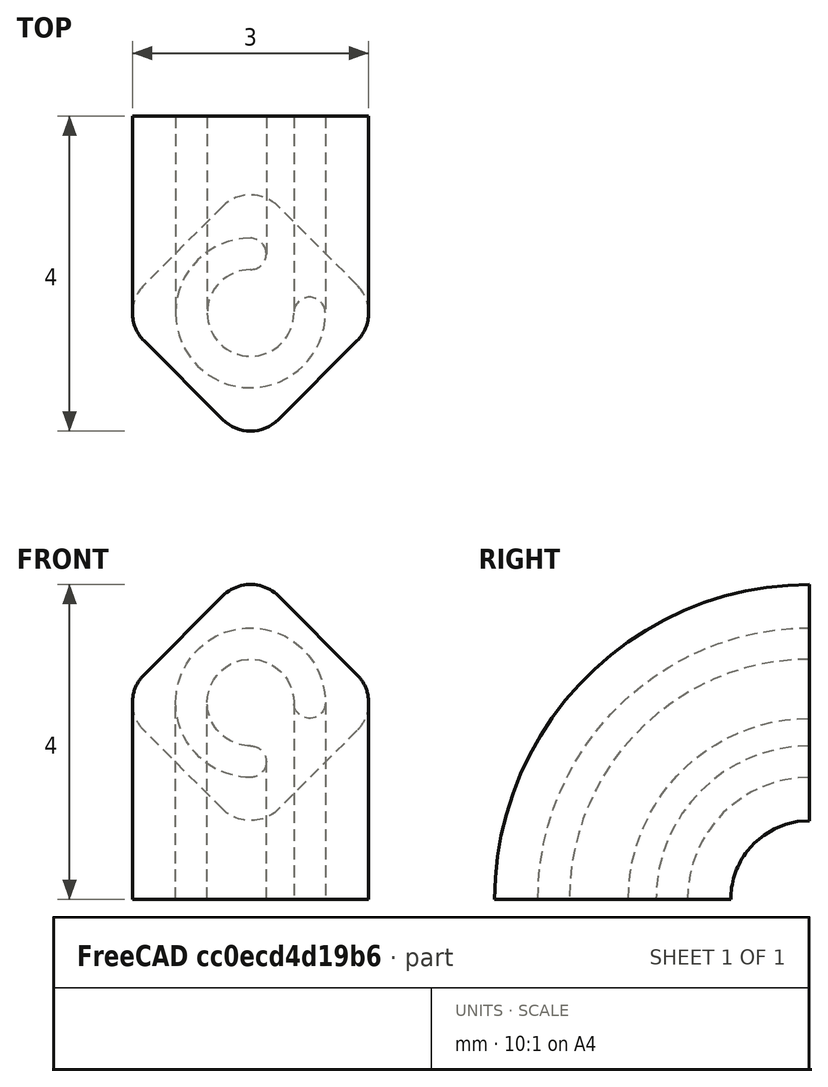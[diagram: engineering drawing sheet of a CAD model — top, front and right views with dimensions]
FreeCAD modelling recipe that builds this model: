
FCSTD DOCUMENT  (FreeCAD 1.0R39109 (Git))
Label: diffusor
License: All rights reserved
LicenseURL: https://en.wikipedia.org/wiki/All_rights_reserved
objects: Sketcher::SketchObject×2, App::VarSet×1, PartDesign::AdditivePipe×1, PartDesign::Body×1
note: 8 computed .brp shape members not serialized (recipe doc carries the construction recipe); baked Part::Feature solids carry a one-line shape summary decoded from their .brp

FEATURE [Sketcher::SketchObject] Sketch  label="diffusor section"
  ArcFitTolerance = 1e-06
  AttachmentSupport = -> [XY_Plane]
  FullyConstrained = true
  MakeInternals = false
  MapMode = 5
  expr: Constraints[11] = VarSet.extension * 0.5
  expr: Constraints[16] = VarSet.extension
  expr: Constraints[17] = VarSet.extension
  expr: Constraints[23] = VarSet.extension * 0.75
  expr: Constraints[24] = VarSet.extension * 0.2
  sketch-geometry (12):
    g0: LineSegment StartX=1.35355 StartY=0.353553 StartZ=0 EndX=0.353553 EndY=1.35355 EndZ=0
    g1: LineSegment StartX=-0.353553 StartY=1.35355 StartZ=0 EndX=-1.35355 EndY=0.353553 EndZ=0
    g2: LineSegment StartX=-1.35355 StartY=-0.353553 StartZ=0 EndX=-0.353553 EndY=-1.35355 EndZ=0
    g3: LineSegment StartX=0.353553 StartY=-1.35355 StartZ=0 EndX=1.35355 EndY=-0.353553 EndZ=0
    g4: ArcOfCircle CenterX=1 CenterY=0 CenterZ=0 NormalX=0 NormalY=0 NormalZ=1 AngleXU=0 Radius=0.5 StartAngle=5.49779 EndAngle=7.06858
    g5: ArcOfCircle CenterX=0 CenterY=1 CenterZ=0 NormalX=0 NormalY=0 NormalZ=1 AngleXU=0 Radius=0.5 StartAngle=0.785398 EndAngle=2.35619
    g6: ArcOfCircle CenterX=-1 CenterY=0 CenterZ=0 NormalX=0 NormalY=0 NormalZ=1 AngleXU=0 Radius=0.5 StartAngle=2.35619 EndAngle=3.92699
    g7: ArcOfCircle CenterX=0 CenterY=-1 CenterZ=0 NormalX=0 NormalY=0 NormalZ=1 AngleXU=0 Radius=0.5 StartAngle=3.92699 EndAngle=5.49779
    g8: ArcOfCircle CenterX=0 CenterY=0 CenterZ=0 NormalX=0 NormalY=0 NormalZ=1 AngleXU=0 Radius=0.95 StartAngle=1.5708 EndAngle=6.28319
    g9: ArcOfCircle CenterX=0.75 CenterY=0 CenterZ=0 NormalX=0 NormalY=0 NormalZ=1 AngleXU=0 Radius=0.2 StartAngle=-4.237e-13 EndAngle=3.14159
    g10: ArcOfCircle CenterX=0 CenterY=0.75 CenterZ=0 NormalX=0 NormalY=0 NormalZ=1 AngleXU=0 Radius=0.2 StartAngle=4.71239 EndAngle=7.85398
    g11: ArcOfCircle CenterX=0 CenterY=0 CenterZ=0 NormalX=0 NormalY=0 NormalZ=1 AngleXU=0 Radius=0.55 StartAngle=1.5708 EndAngle=6.28319
  constraints (28):
    c: Tangent(g0,g4) = -1.5708
    c: Tangent(g0,g5) = -1.5708
    c: Tangent(g1,g5) = -1.5708
    c: Tangent(g1,g6) = -1.5708
    c: Tangent(g2,g6) = -1.5708
    c: Tangent(g2,g7) = -1.5708
    c: Tangent(g3,g7) = -1.5708
    c: Tangent(g3,g4) = -1.5708
    c: Parallel(g0,g2)
    c: Parallel(g1,g3)
    c: Equal(g4,g5)
    c: Radius(g5) = 0.5
    c: Symmetric(g5,g7,g-1)
    c: Symmetric(g6,g4,g-2)
    c: PointOnObject(g6,g-1)
    c: PointOnObject(g5,g-2)
    c: Distance(g-1,g6) = 1
    c: Distance(g-1,g5) = 1
    c: Coincident(g8,g11)
    c: Tangent(g11,g10) = 1.5708
    c: Tangent(g11,g9) = 1.5708
    c: Tangent(g8,g10) = -1.5708
    c: Tangent(g8,g9) = -1.5708
    c: Distance(g8,g10) = 0.75
    c: Radius(g10) = 0.2
    c: Coincident(g8,g-1)
    c: PointOnObject(g9,g-1)
    c: PointOnObject(g10,g-2)
FEATURE [App::VarSet] VarSet
  extension = 1
FEATURE [Sketcher::SketchObject] Sketch001  label="extrusion arc path"
  ArcFitTolerance = 1e-06
  AttachmentSupport = -> [YZ_Plane]
  FullyConstrained = true
  MakeInternals = false
  MapMode = 5
  Placement = pos=(0,0,0) rot=(0.57735,0.57735,0.57735;2.0944rad)
  expr: Constraints[0] = VarSet.extension * 2.5
  sketch-geometry (1):
    g0: ArcOfCircle CenterX=2.5 CenterY=0 CenterZ=0 NormalX=0 NormalY=0 NormalZ=1 AngleXU=0 Radius=2.5 StartAngle=1.5708 EndAngle=3.14159
  constraints (4):
    c: Radius(g0) = 2.5
    c: Angle(g0) = 1.5708
    c: PointOnObject(g0,g-1)
    c: Coincident(g0,g-1)
FEATURE [PartDesign::AdditivePipe] AdditivePipe  label="diffusor"
  AuxilleryCurvelinear = true
  AuxillerySpineTangent = false
  Binormal = (0,0,0)
  Mode = 0
  Profile = -> Sketch [Edge1]
  Refine = true
  Spine = -> Sketch001
  SpineTangent = false
  Suppressed = false
  Transformation = 0
  Transition = 0
FEATURE [PartDesign::Body] Body
  AllowCompound = false
  Group = -> [Sketch,Sketch001,AdditivePipe]
  Origin = -> Origin
  Tip = -> AdditivePipe
